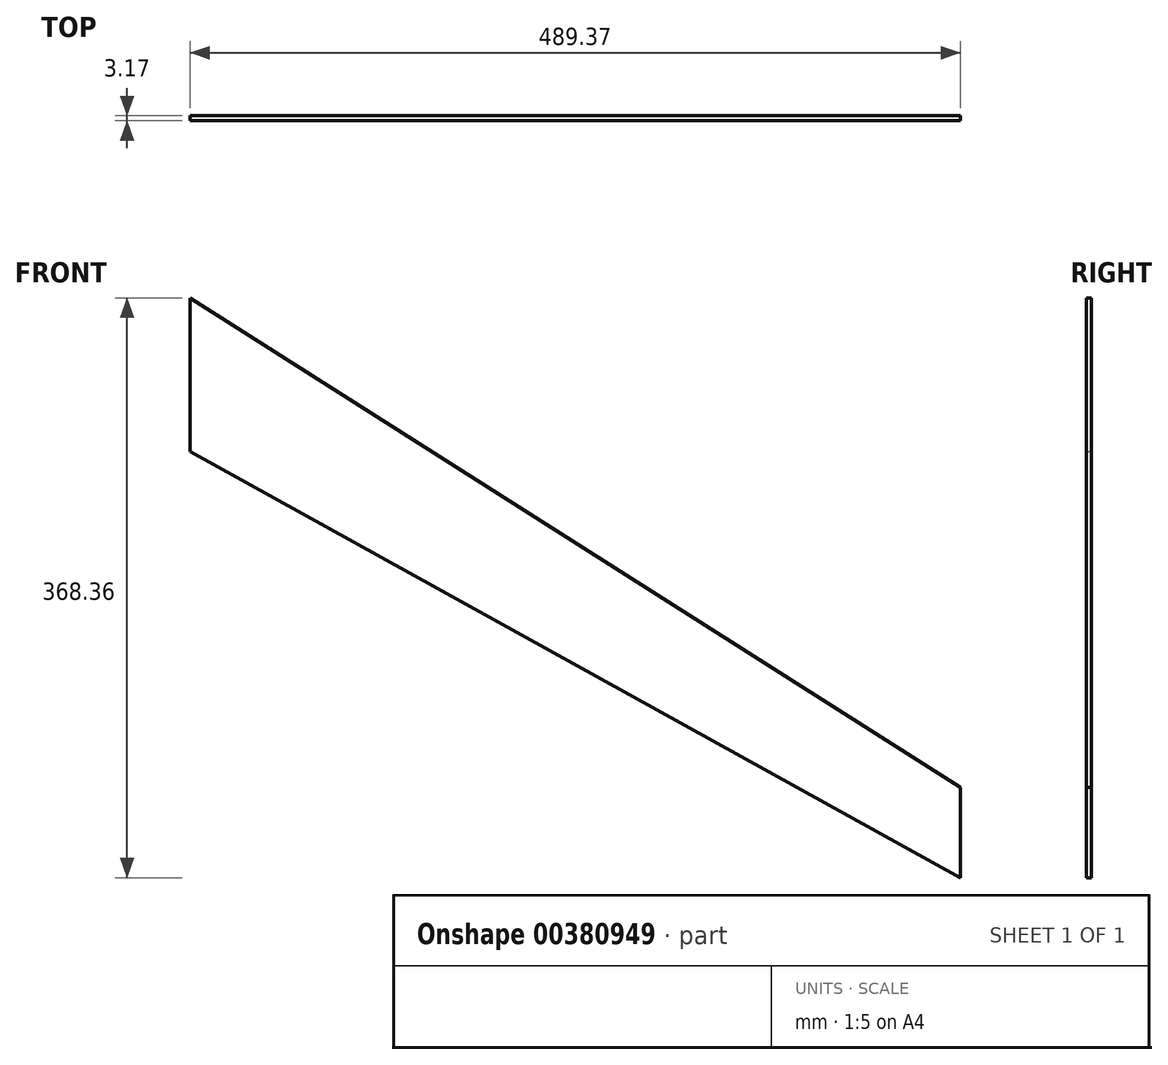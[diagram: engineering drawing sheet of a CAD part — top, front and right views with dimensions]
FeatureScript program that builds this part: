
annotation { "Feature Type Name" : "Feature", "Feature Type Description" : "" }
export const myFeature = defineFeature(function(context is Context, id is Id, definition is map)
    precondition{}
    {
        {
            var Q0;
            Q0=qCreatedBy(makeId("Front.planeOp"),FACE);
            var sketch = newSketch(context, id + "F0", { "sketchPlane" : qUnion([Q0])});
            skLineSegment(sketch, "E0", {"start": v(0, 0) * mm, "end": v(0, 97.54) * mm});
            skLineSegment(sketch, "E1", {"start": v(0, 97.54) * mm, "end": v(489.37, -213.41) * mm});
            skLineSegment(sketch, "E2", {"start": v(489.37, -213.41) * mm, "end": v(489.37, -270.82) * mm});
            skLineSegment(sketch, "E3", {"start": v(0, 0) * mm, "end": v(489.37, -270.82) * mm});
            skSolve(sketch);
        }
        {
            var Q0;
            Q0=qSketchRegion(id+"F0",true);
            extrude(context, id + "F1", {"entities" : qUnion([Q0]), "depth" : 3.17 * mm});
        }
    });
